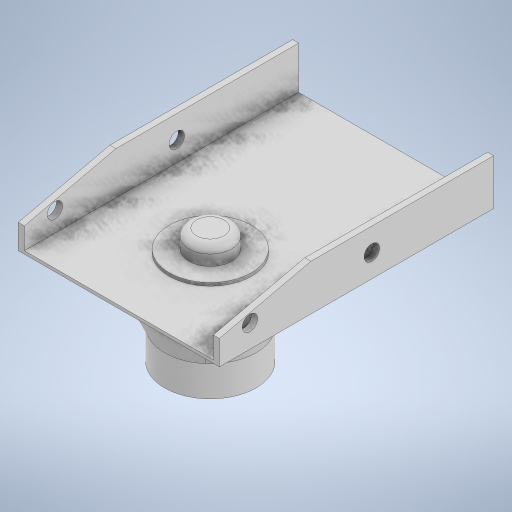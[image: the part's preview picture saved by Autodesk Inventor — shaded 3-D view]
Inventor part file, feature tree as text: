
AUTODESK INVENTOR PART (.ipt)
format: ipt  version: 2023 (Build 270158030, 158C)  size: 408,576 bytes
history: native  units: in
note: dims shown in document units (in); Inventor stores cm internally (conversion verified against a paired STEP export)
features: sketch x10, extrude x8, plane x1, loft x1, fillet x1
ambient origin geometry x8: Origin, YZ Plane, XZ Plane, XY Plane, X Axis, Y Axis, Z Axis, Center Point
bodies: Solid1 (feature_tree)
feature tree (21):
  extrude  "Extrusion1"  Depth=1.5in
  extrude  "Extrusion2"  Depth=0.5in
  sketch  "Sketch3"  dims[d5=0.95in d6=0.05in d7=0.0in]
  plane  "Work Plane1"
  loft  "Loft1"
  extrude  "Extrusion3"  Depth=1.5in
  extrude  "Extrusion4"  Depth=1.0in
  extrude  "Extrusion5"  Depth=0.125in
  extrude  "Extrusion6"  Depth=1.0in
  extrude  "Extrusion7"  Depth=4.5in
  extrude  "Extrusion8"  Depth=0.05in TaperAngle=0.0deg
  fillet  "Fillet1"  Radius=0.1in
  sketch  "Sketch1"  dims[d0=1.35in d1=1.5in]
  sketch  "Sketch2"  dims[d2=0.5in d3=0.0in d4=1.35in]
  sketch  "Sketch4"  dims[d8=1.5in d9=1.5in]
  sketch  "Sketch6"  dims[d10=1.0in d12=2.0in]
  sketch  "Sketch7"  dims[d13=2.0in d14=0.125in]
  sketch  "Sketch8"  dims[d15=1.0in d16=1.0in]
  sketch  "Sketch9"  dims[d19=0.0in d20=90.0deg d21=0.0in d22=90.0deg d27=4.5in]
  sketch  "Sketch10"  dims[d28=3.3in d29=0.05in d30=0.0in d31=0.1in]
  sketch  "Sketch11"  dims[d32=0.1in d33=0.7in d34=0.0in d35=1.5in d36=90.0deg d37=1.65in d38=90.0deg d39=3.2in d40=1.0in d41=1.0in d42=0.25in d43=0.25in d44=3.3in d45=0.0in d46=1.1475in d47=1.5in d48=3.3in d49=0.0in d50=1.35in d51=0.05in d52=0.0in d53=0.7in d54=0.3in d55=0.0in d56=0.125in]
